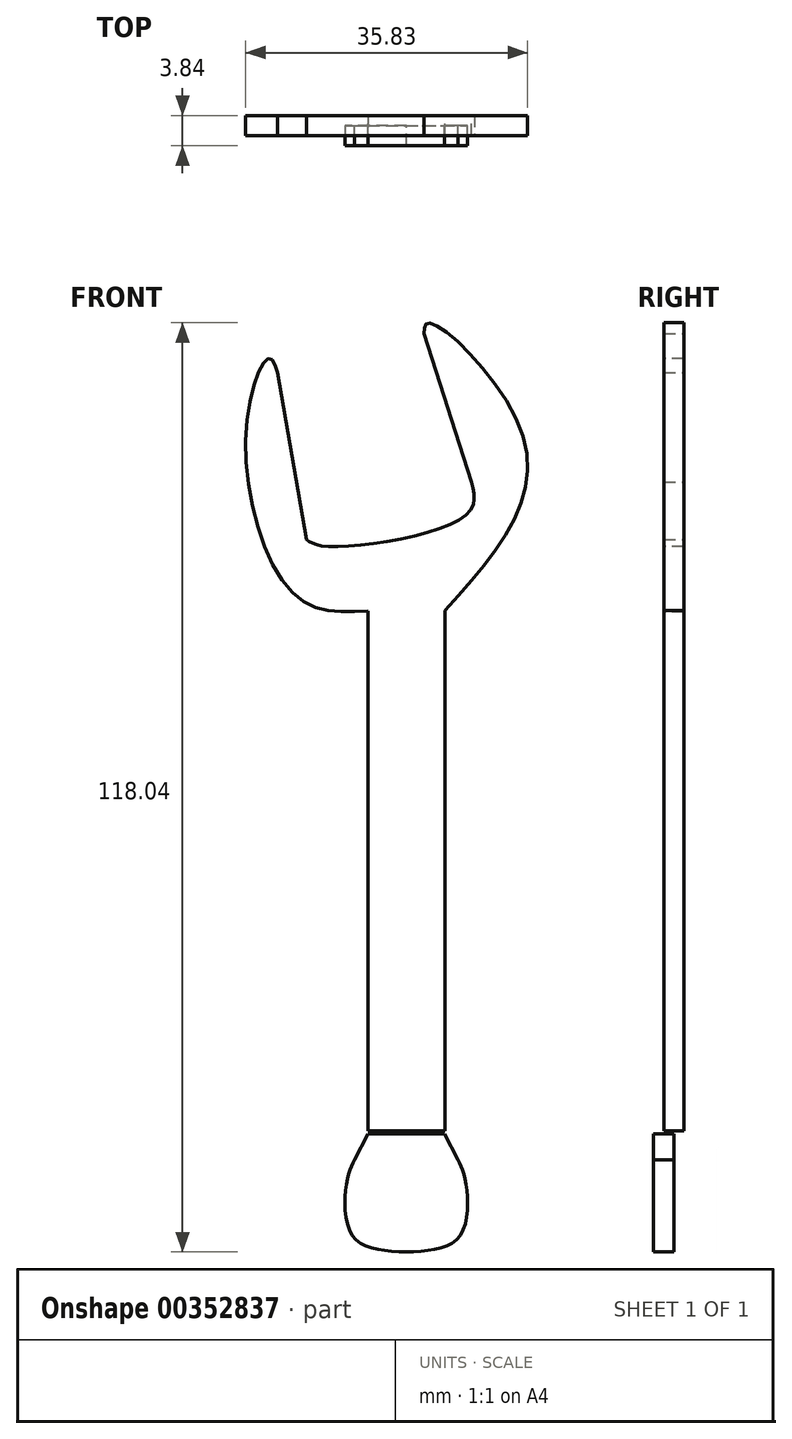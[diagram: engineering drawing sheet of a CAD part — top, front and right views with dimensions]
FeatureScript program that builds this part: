
annotation { "Feature Type Name" : "Feature", "Feature Type Description" : "" }
export const myFeature = defineFeature(function(context is Context, id is Id, definition is map)
    precondition{}
    {
        {
            var Q0;
            Q0=qCreatedBy(makeId("Front.planeOp"),FACE);
            var sketch = newSketch(context, id + "F0", { "sketchPlane" : qUnion([Q0])});
            skCircle(sketch, "E0", {"center": v(0, -69.33) * mm, "radius": 4.13 * mm});
            skFitSpline(sketch, "E1", {"points": [v(0, -74.74) * mm, v(-6.7, -72.82) * mm, v(-7.57, -65.94) * mm, v(-6.57, -63.01) * mm], "startDerivative": vector(-21.54, 1) * mm, "endDerivative": vector(4.56, 9.56) * mm});
            skLineSegment(sketch, "E2", {"start": v(-6.57, -63.01) * mm, "end": v(-4.87, -59.71) * mm});
            skFitSpline(sketch, "E3.MirrorCS", {"points": [v(0, -74.74) * mm, v(6.7, -72.82) * mm, v(7.57, -65.94) * mm, v(6.57, -63.01) * mm], "startDerivative": vector(21.54, 1) * mm, "endDerivative": vector(-4.56, 9.56) * mm});
            skLineSegment(sketch, "E4.MirrorCS", {"start": v(6.57, -63.01) * mm, "end": v(4.87, -59.71) * mm});
            skLineSegment(sketch, "E5", {"start": v(-4.87, -59.71) * mm, "end": v(4.87, -59.71) * mm});
            skSolve(sketch);
        }
        {
            var Q0;
            Q0=makeQuery(id+"F0.imprint","IMPRINT",FACE,{"disambiguationData":[TD([[makeQuery(id+"F0.imprint","IMPRINT",EDGE,{"derivedFrom":sQuery(id+"F0.wireOp",EDGE,"E0")}),1.0]])]});
            var Q1;
            Q1=makeQuery(id+"F0.imprint","IMPRINT",FACE,{"disambiguationData":[TD([[makeQuery(id+"F0.imprint","IMPRINT",EDGE,{"derivedFrom":sQuery(id+"F0.wireOp",EDGE,"E0")}),-1.0]])]});
            extrude(context, id + "F1", {"entities" : qUnion([Q0, Q1]), "depth" : 2.57 * mm});
        }
        {
            var Q0;
            Q0=qCreatedBy(makeId("Front.planeOp"),FACE);
            var sketch = newSketch(context, id + "F2", { "sketchPlane" : qUnion([Q0])});
            skLineSegment(sketch, "E6", {"start": v(-4.87, -59.71) * mm, "end": v(-4.87, 6.7) * mm});
            skLineSegment(sketch, "E7.MirrorCS", {"start": v(4.87, -59.71) * mm, "end": v(4.87, 6.7) * mm});
            skFitSpline(sketch, "E8", {"points": [v(-4.87, 6.7) * mm, v(-14.13, 8.7) * mm, v(-20.36, 29.49) * mm, v(-17.43, 38.79) * mm, v(-16.33, 36.95) * mm], "startDerivative": vector(-39.55, -2.43) * mm, "endDerivative": vector(8.04, -23.21) * mm});
            skLineSegment(sketch, "E9", {"start": v(-16.33, 36.95) * mm, "end": v(-12.66, 15.79) * mm});
            skFitSpline(sketch, "E10", {"points": [v(-12.66, 15.79) * mm, v(-10.1, 14.88) * mm, v(7.65, 18.92) * mm, v(8.26, 23.08) * mm], "startDerivative": vector(7.45, -5.8) * mm, "endDerivative": vector(-4.69, 16.96) * mm});
            skLineSegment(sketch, "E11", {"start": v(8.26, 23.08) * mm, "end": v(2.26, 41.92) * mm});
            skFitSpline(sketch, "E12", {"points": [v(2.26, 41.92) * mm, v(2.8, 43.3) * mm, v(15.02, 28.16) * mm, v(4.87, 6.7) * mm], "startDerivative": vector(0.18, 17.36) * mm, "endDerivative": vector(-39.41, -43.76) * mm});
            skFitSpline(sketch, "E13", {"points": [v(-4.87, 6.7) * mm, v(4.87, 6.7) * mm], "startDerivative": vector(9.74, 0) * mm, "endDerivative": vector(9.74, 0) * mm});
            skSolve(sketch);
        }
        {
            var Q0;
            Q0=makeQuery(id+"F2.imprint","IMPRINT",FACE,{"disambiguationData":[TD([[makeQuery(id+"F2.imprint","IMPRINT",EDGE,{"derivedFrom":sQuery(id+"F2.wireOp",EDGE,"E8")}),-1.0]])]});
            extrude(context, id + "F3", {"entities" : qUnion([Q0]), "endBound" : BoundingType.SYMMETRIC, "depth" : 2.54 * mm});
        }
        {
            var Q0;
            Q0=qCreatedBy(makeId("Front.planeOp"),FACE);
            var sketch = newSketch(context, id + "F4", { "sketchPlane" : qUnion([Q0])});
            skLineSegment(sketch, "E14", {"start": v(-4.84, 6.75) * mm, "end": v(4.9, 6.75) * mm});
            skLineSegment(sketch, "E15", {"start": v(4.9, 6.75) * mm, "end": v(4.9, -59.34) * mm});
            skLineSegment(sketch, "E16", {"start": v(4.9, -59.34) * mm, "end": v(-4.85, -59.34) * mm});
            skLineSegment(sketch, "E17", {"start": v(-4.85, -59.34) * mm, "end": v(-4.84, 6.75) * mm});
            skSolve(sketch);
        }
        {
            var Q0;
            Q0=makeQuery(id+"F4.imprint","IMPRINT",FACE,{"disambiguationData":[TD([[makeQuery(id+"F4.imprint","IMPRINT",EDGE,{"derivedFrom":sQuery(id+"F4.wireOp",EDGE,"E14")}),-1.0]])]});
            extrude(context, id + "F5", {"entities" : qUnion([Q0]), "operationType" : NewBodyOperationType.ADD, "endBound" : BoundingType.SYMMETRIC, "depth" : 2.54 * mm});
        }
    });
